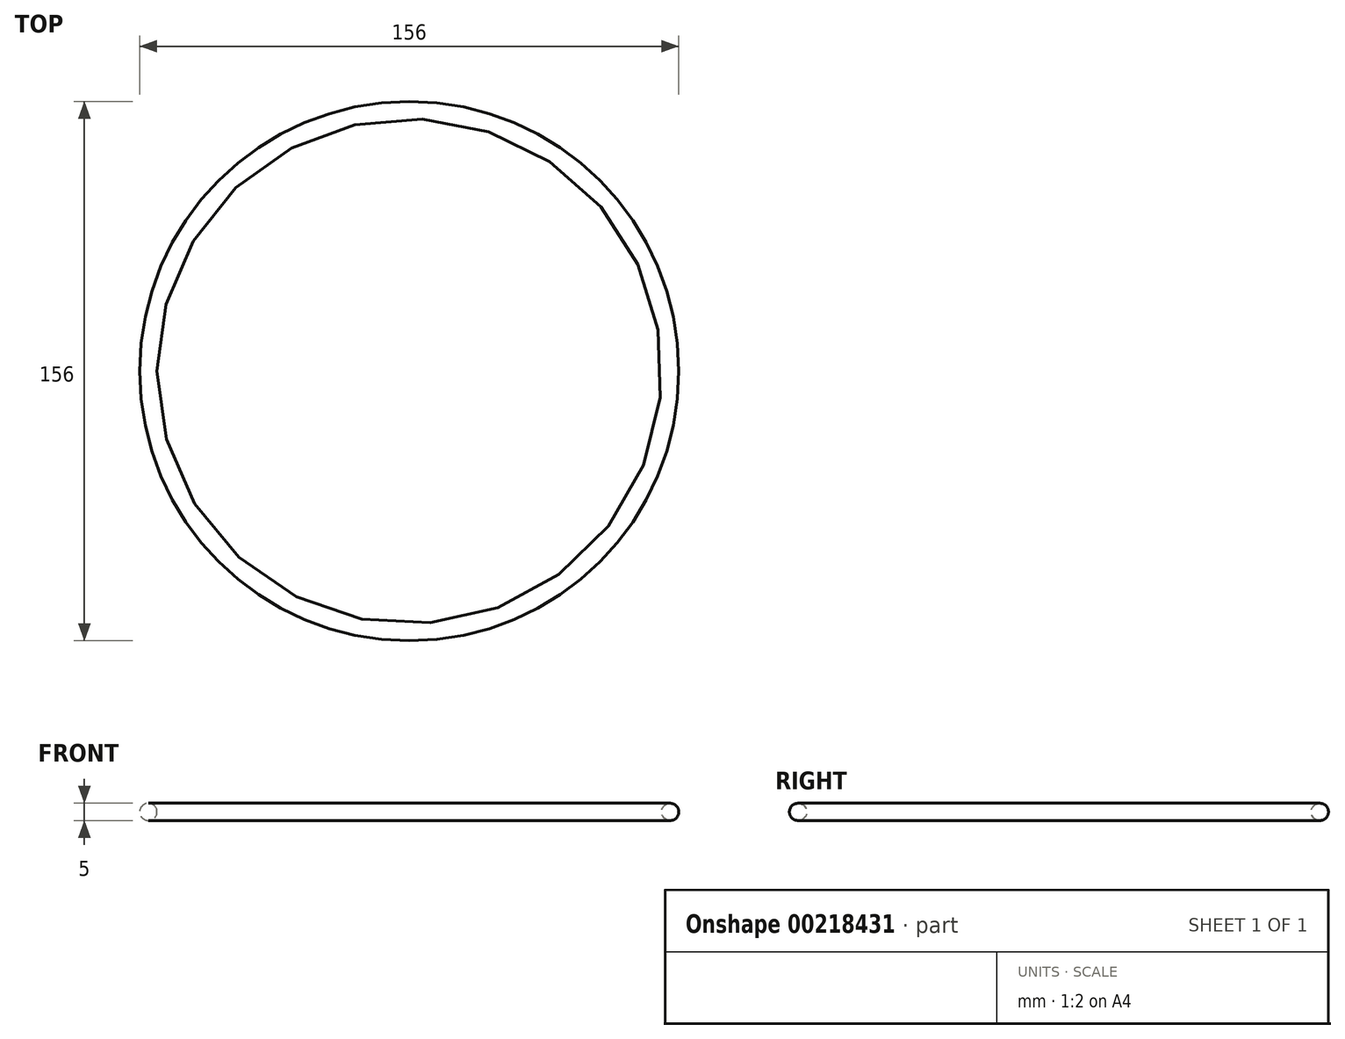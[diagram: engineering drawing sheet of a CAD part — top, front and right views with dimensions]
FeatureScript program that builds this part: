
annotation { "Feature Type Name" : "Feature", "Feature Type Description" : "" }
export const myFeature = defineFeature(function(context is Context, id is Id, definition is map)
    precondition{}
    {
        {
            var Q0;
            Q0=qCreatedBy(makeId("Front.planeOp"),FACE);
            var sketch = newSketch(context, id + "F0", { "sketchPlane" : qUnion([Q0])});
            skLineSegment(sketch, "E0", {"start": v(0, 0) * mm, "end": v(0, 50) * mm});
            skSolve(sketch);
        }
        {
            var Q0;
            Q0=qCreatedBy(makeId("Front.planeOp"),FACE);
            var sketch = newSketch(context, id + "F1", { "sketchPlane" : qUnion([Q0])});
            skCircle(sketch, "E1", {"center": v(-75.5, 0) * mm, "radius": 2.5 * mm});
            skSolve(sketch);
        }
        {
            var Q0;
            Q0=makeQuery(id+"F1.imprint","IMPRINT",FACE,{"disambiguationData":[TD([[makeQuery(id+"F1.imprint","IMPRINT",EDGE,{"derivedFrom":sQuery(id+"F1.wireOp",EDGE,"E1")}),1.0]])]});
            var Q1;
            Q1=sQuery(id+"F0.wireOp",EDGE,"E0");
            revolve(context, id + "F2", {"entities" : qUnion([Q0]), "axis" : qUnion([Q1]), "revolveType" : RevolveType.FULL});
        }
    });
